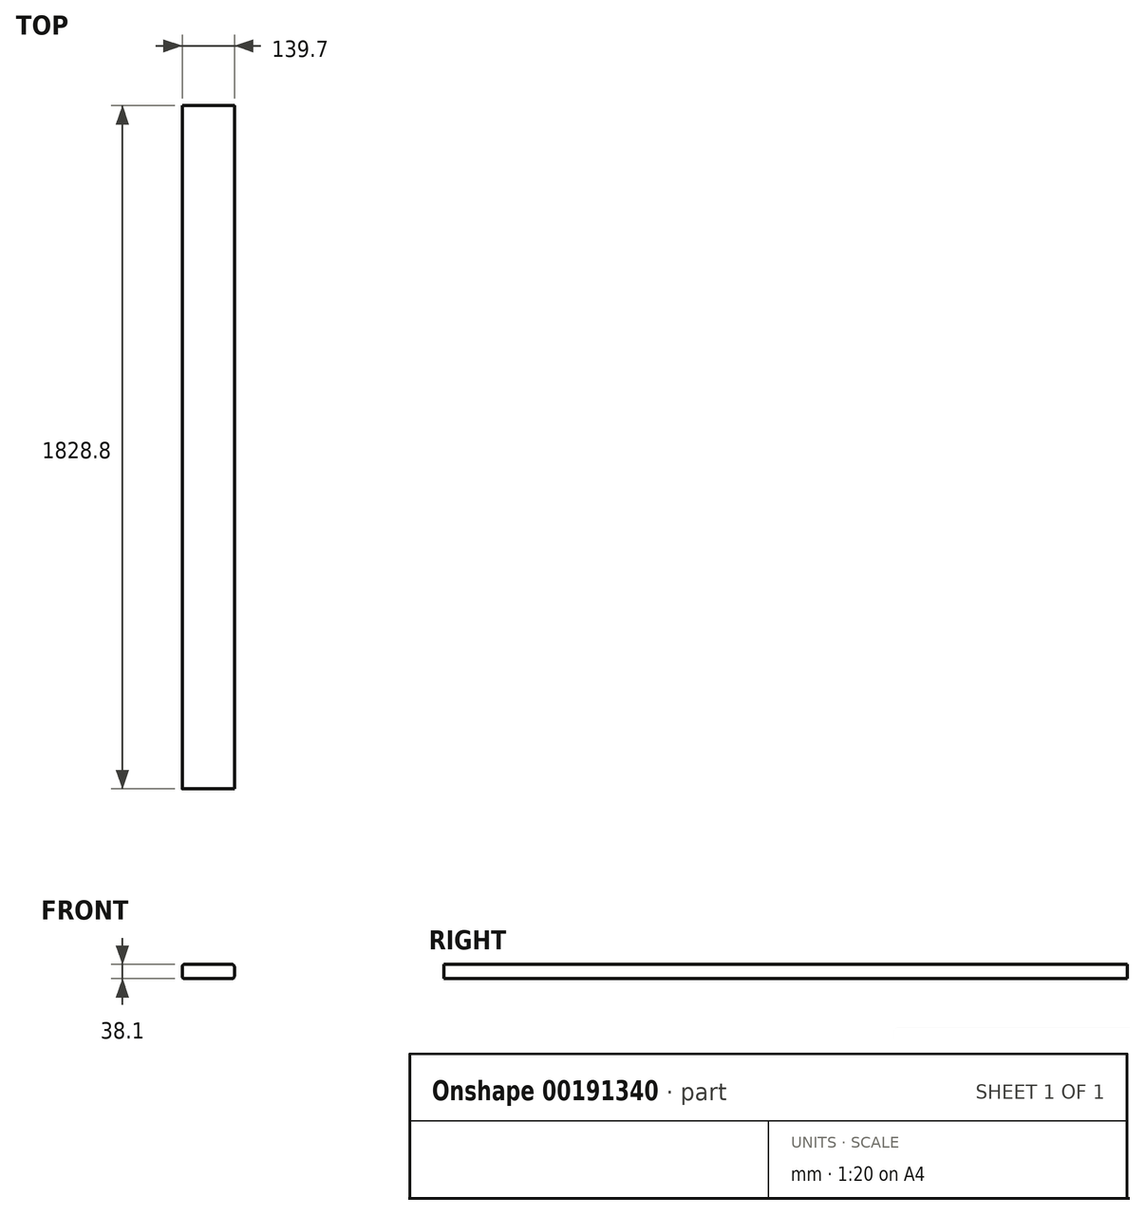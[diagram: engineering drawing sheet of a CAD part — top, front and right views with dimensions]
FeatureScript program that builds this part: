
annotation { "Feature Type Name" : "Feature", "Feature Type Description" : "" }
export const myFeature = defineFeature(function(context is Context, id is Id, definition is map)
    precondition{}
    {
        {
            var Q0;
            Q0=qCreatedBy(makeId("Front.planeOp"),FACE);
            var sketch = newSketch(context, id + "F0", { "sketchPlane" : qUnion([Q0])});
            skLineSegment(sketch, "E0.bottom", {"start": v(-63.5, 19.05) * mm, "end": v(63.5, 19.05) * mm});
            skLineSegment(sketch, "E0.top", {"start": v(-63.5, -19.05) * mm, "end": v(63.5, -19.05) * mm});
            skLineSegment(sketch, "E0.left", {"start": v(-69.85, 12.7) * mm, "end": v(-69.85, -12.7) * mm});
            skLineSegment(sketch, "E0.right", {"start": v(69.85, 12.7) * mm, "end": v(69.85, -12.7) * mm});
            skPoint(sketch, "E0.middle", {"position": v(0, 0) * mm});
            skPoint(sketch, "E1.visualSharp", {"position": v(-69.85, 19.05) * mm});
            skArc(sketch, "E1.filletArc", {"start": v(-63.5, 19.05) * mm, "mid": v(-68, 17.2) * mm, "end": v(-69.85, 12.7) * mm});
            skPoint(sketch, "E2.visualSharp", {"position": v(-69.85, -19.05) * mm});
            skArc(sketch, "E2.filletArc", {"start": v(-69.85, -12.7) * mm, "mid": v(-68, -17.2) * mm, "end": v(-63.5, -19.05) * mm});
            skPoint(sketch, "E3.visualSharp", {"position": v(69.85, -19.05) * mm});
            skArc(sketch, "E3.filletArc", {"start": v(63.5, -19.05) * mm, "mid": v(68, -17.2) * mm, "end": v(69.85, -12.7) * mm});
            skPoint(sketch, "E4.visualSharp", {"position": v(69.85, 19.05) * mm});
            skArc(sketch, "E4.filletArc", {"start": v(69.85, 12.7) * mm, "mid": v(68, 17.2) * mm, "end": v(63.5, 19.05) * mm});
            skSolve(sketch);
        }
        {
            var Q0;
            Q0=makeQuery(id+"F0.imprint","IMPRINT",FACE,{"disambiguationData":[TD([[makeQuery(id+"F0.imprint","IMPRINT",EDGE,{"derivedFrom":sQuery(id+"F0.wireOp",EDGE,"E0.bottom")}),-1.0]])]});
            extrude(context, id + "F1", {"entities" : qUnion([Q0]), "depth" : 1828.8 * mm});
        }
    });
